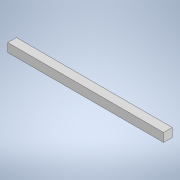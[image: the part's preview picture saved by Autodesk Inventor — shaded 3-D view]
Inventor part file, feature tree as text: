
AUTODESK INVENTOR PART (.ipt)
format: ipt  version: 2020 (Build 240168000, 168)  size: 98,816 bytes
history: native  units: mm
features: other x1, extrude x1, sketch x1
ambient origin geometry x8: Origin, YZ Plane, XZ Plane, XY Plane, X Axis, Y Axis, Z Axis, Center Point
bodies: Solid1 (feature_tree)
feature tree (3):
  other  "<userpath>\Documents\Development\paragon-printer\Paragon Printer Parameters.xlsx"
  extrude  "Extrusion1"  Depth=20.0mm
  sketch  "Sketch1"  dims[d0=20.0mm d1=20.0mm d2=360.0mm d3=0.0mm]
